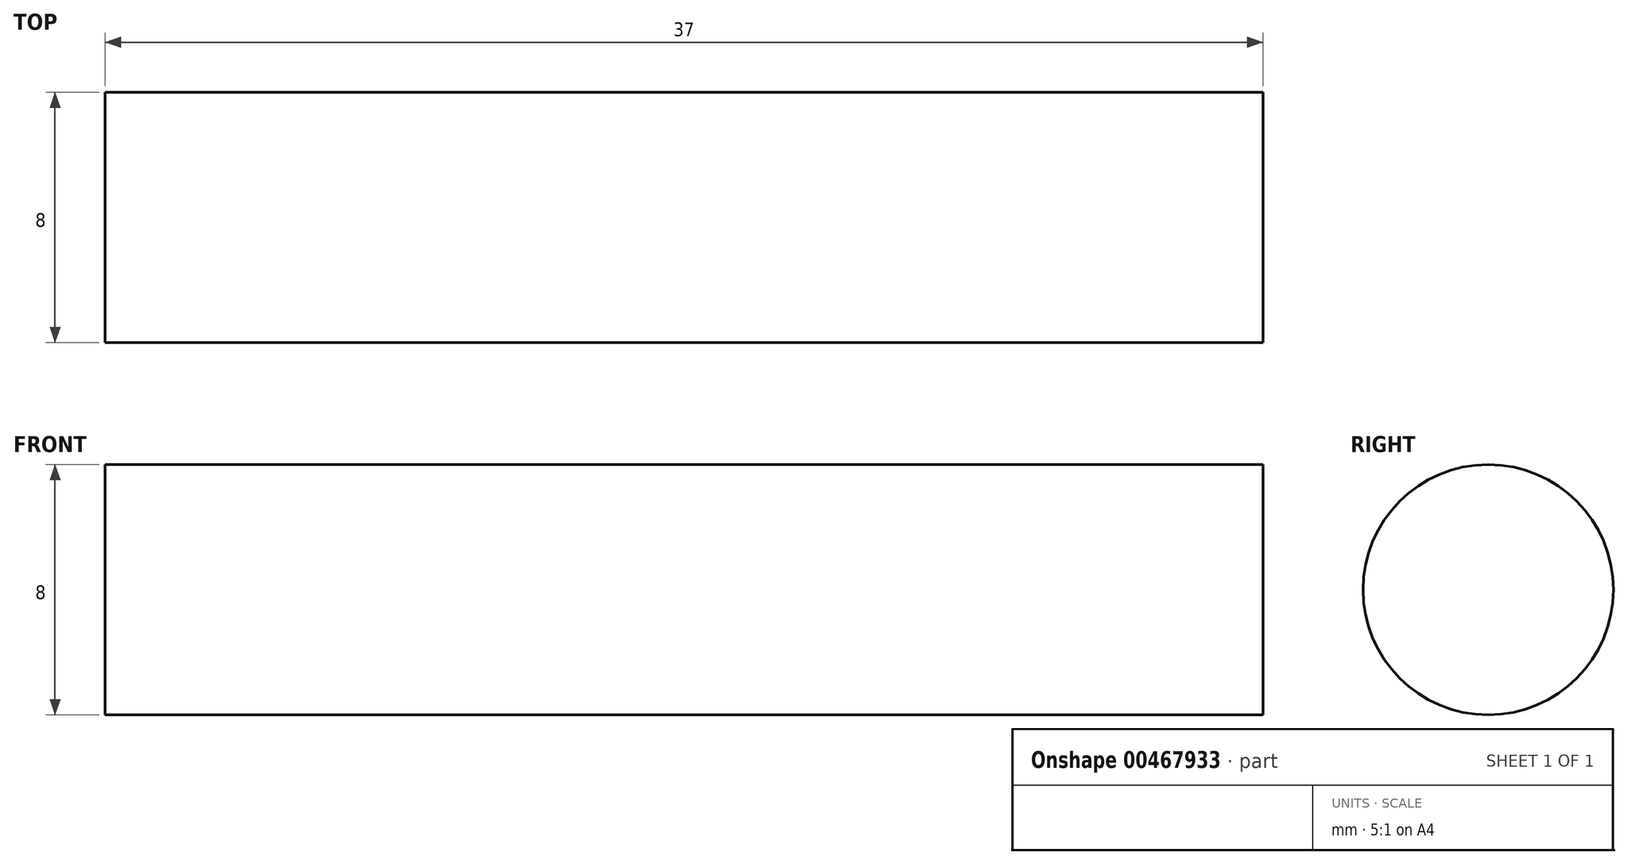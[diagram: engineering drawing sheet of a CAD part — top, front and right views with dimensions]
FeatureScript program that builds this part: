
annotation { "Feature Type Name" : "Feature", "Feature Type Description" : "" }
export const myFeature = defineFeature(function(context is Context, id is Id, definition is map)
    precondition{}
    {
        {
            var Q0;
            Q0=qCreatedBy(makeId("Right.planeOp"),FACE);
            var sketch = newSketch(context, id + "F0", { "sketchPlane" : qUnion([Q0])});
            skCircle(sketch, "E0", {"center": v(0, 0) * mm, "radius": 4 * mm});
            skPoint(sketch, "E1", {"position": v(-4, 0) * mm});
            skPoint(sketch, "E2", {"position": v(4, 0) * mm});
            skLineSegment(sketch, "E3", {"start": v(-4, 0) * mm, "end": v(4, 0) * mm});
            skSolve(sketch);
        }
        {
            var Q0;
            Q0 = qSketchRegion(id + "F0", true);
            extrude(context, id + "F1", {"entities" : qUnion([Q0]), "endBound" : BoundingType.SYMMETRIC, "depth" : 37 * mm});
        }
    });
